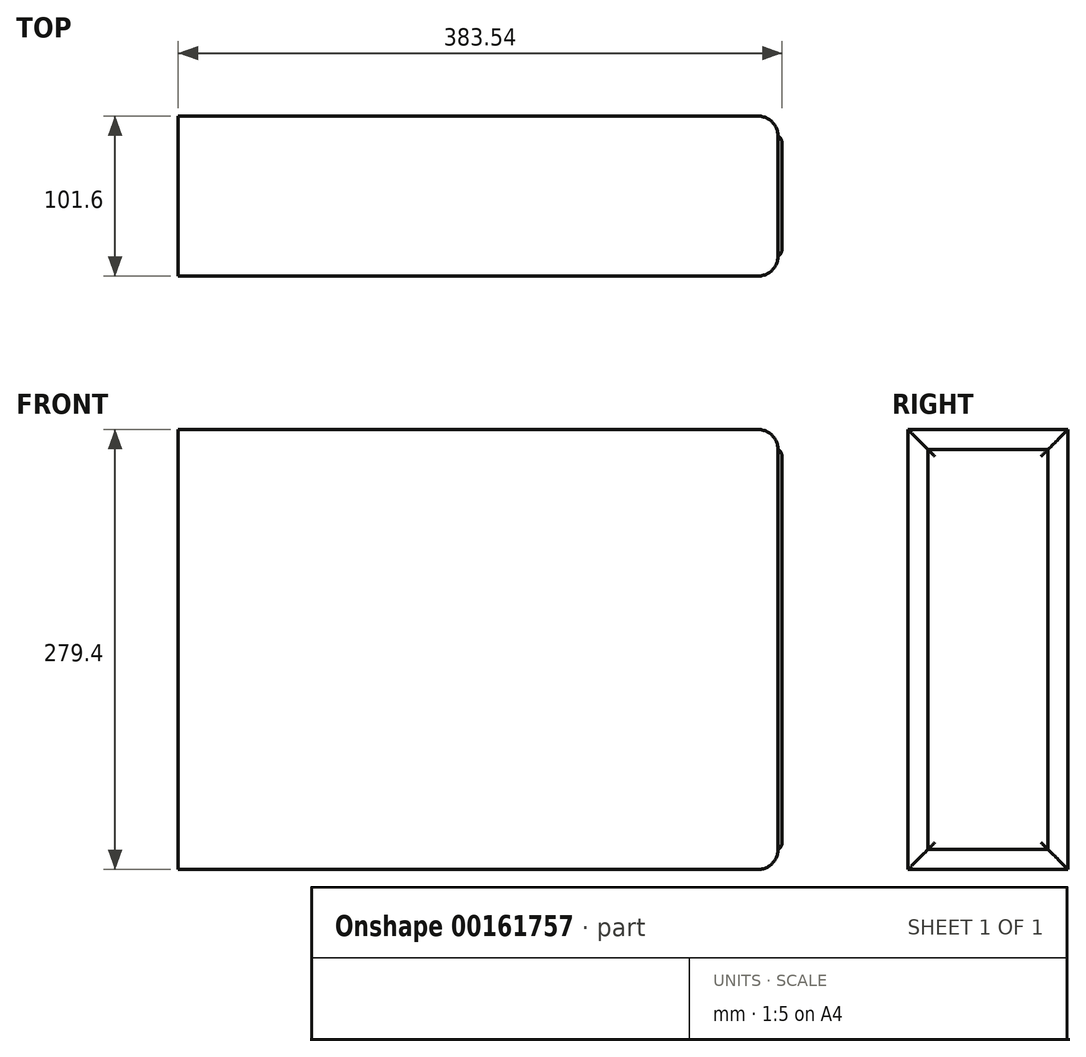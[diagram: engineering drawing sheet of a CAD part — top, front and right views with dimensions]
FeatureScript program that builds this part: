
annotation { "Feature Type Name" : "Feature", "Feature Type Description" : "" }
export const myFeature = defineFeature(function(context is Context, id is Id, definition is map)
    precondition{}
    {
        {
            var Q0;
            Q0=qCreatedBy(makeId("Front.planeOp"),FACE);
            var sketch = newSketch(context, id + "F0", { "sketchPlane" : qUnion([Q0])});
            skLineSegment(sketch, "E0.bottom", {"start": v(-189.27, -107.22) * mm, "end": v(191.73, -107.22) * mm});
            skLineSegment(sketch, "E0.top", {"start": v(-189.27, 172.18) * mm, "end": v(191.73, 172.18) * mm});
            skLineSegment(sketch, "E0.left", {"start": v(-189.27, -107.22) * mm, "end": v(-189.27, 172.18) * mm});
            skLineSegment(sketch, "E0.right", {"start": v(191.73, -107.22) * mm, "end": v(191.73, 172.18) * mm});
            skSolve(sketch);
        }
        {
            var Q0;
            Q0 = qSketchRegion(id + "F0", true);
            extrude(context, id + "F1", {"entities" : qUnion([Q0]), "depth" : 101.6 * mm});
        }
        {
            var Q0;
            Q0=makeQuery(id+"F1.opExtrude","SWEPT_EDGE",EDGE,{"disambiguationData":[OSD([sQuery(id+"F0.wireOp",EDGE,"E0.top"),sQuery(id+"F0.wireOp",EDGE,"E0.right")])]});
            var Q1;
            Q1=makeQuery(id+"F1.opExtrude","CAP_EDGE",EDGE,{"disambiguationData":[OSD([sQuery(id+"F0.wireOp",EDGE,"E0.right")])],"isStart":false});
            var Q2;
            Q2=makeQuery(id+"F1.opExtrude","SWEPT_EDGE",EDGE,{"disambiguationData":[OSD([sQuery(id+"F0.wireOp",EDGE,"E0.bottom"),sQuery(id+"F0.wireOp",EDGE,"E0.right")])]});
            var Q3;
            Q3=makeQuery(id+"F1.opExtrude","CAP_EDGE",EDGE,{"disambiguationData":[OSD([sQuery(id+"F0.wireOp",EDGE,"E0.right")])],"isStart":true});
            fillet(context, id + "F2", {"entities" : qUnion([Q0, Q1, Q2, Q3]), "radius" : 12.7 * mm, "tangentPropagation" : true, "allowEdgeOverflow" : false});
        }
        {
            var Q0;
            Q0=makeQuery(id+"F1.opExtrude","SWEPT_FACE",FACE,{"disambiguationData":[OSD([sQuery(id+"F0.wireOp",EDGE,"E0.right")])]});
            extrude(context, id + "F3", {"entities" : qUnion([Q0]), "operationType" : NewBodyOperationType.ADD, "depth" : 2.54 * mm});
        }
        {
            var Q0;
            Q0=makeQuery(id+"F3.opExtrude","CAP_EDGE",EDGE,{"disambiguationData":[OSD([sQuery(id+"F0.wireOp",EDGE,"E0.top"),sQuery(id+"F0.wireOp",EDGE,"E0.right")])],"isStart":false});
            var Q1;
            {var subQ0=sQuery(id+"F0.wireOp",EDGE,"E0.right");Q1=makeQuery(id+"F3.opExtrude","CAP_EDGE",EDGE,{"disambiguationData":[OSD([subQ0]),TDD([makeQuery(id+"F2.opFillet","BLEND_EDGE",EDGE,{"blendedFrom":[makeQuery(id+"F1.opExtrude","CAP_EDGE",EDGE,{"disambiguationData":[OSD([subQ0])],"isStart":false}),makeQuery(id+"F1.opExtrude","SWEPT_FACE",FACE,{"disambiguationData":[OSD([subQ0])]})],"blendedInto":[makeQuery(id+"F1.opExtrude","SWEPT_FACE",FACE,{"disambiguationData":[OSD([subQ0])]})]})])],"isStart":false});}
            var Q2;
            {var subQ0=sQuery(id+"F0.wireOp",EDGE,"E0.right");Q2=makeQuery(id+"F3.opExtrude","CAP_EDGE",EDGE,{"disambiguationData":[OSD([subQ0]),TDD([makeQuery(id+"F2.opFillet","BLEND_EDGE",EDGE,{"blendedFrom":[makeQuery(id+"F1.opExtrude","CAP_EDGE",EDGE,{"disambiguationData":[OSD([subQ0])],"isStart":true}),makeQuery(id+"F1.opExtrude","SWEPT_FACE",FACE,{"disambiguationData":[OSD([subQ0])]})],"blendedInto":[makeQuery(id+"F1.opExtrude","SWEPT_FACE",FACE,{"disambiguationData":[OSD([subQ0])]})]})])],"isStart":false});}
            var Q3;
            Q3=makeQuery(id+"F3.opExtrude","CAP_EDGE",EDGE,{"disambiguationData":[OSD([sQuery(id+"F0.wireOp",EDGE,"E0.bottom"),sQuery(id+"F0.wireOp",EDGE,"E0.right")])],"isStart":false});
            fillet(context, id + "F4", {"entities" : qUnion([Q0, Q1, Q2, Q3]), "radius" : 5.08 * mm, "tangentPropagation" : true, "allowEdgeOverflow" : false});
        }
    });
